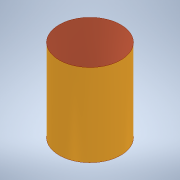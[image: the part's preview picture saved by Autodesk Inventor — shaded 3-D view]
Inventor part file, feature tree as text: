
AUTODESK INVENTOR PART (.ipt)
format: ipt  version: 2020.1 (Build 241239000, 239)  size: 92,672 bytes
history: native  units: mm
features: extrude x1, sketch x1
ambient origin geometry x8: Origin, YZ Plane, XZ Plane, XY Plane, X Axis, Y Axis, Z Axis, Center Point
bodies: Solid1 (feature_tree)
feature tree (2):
  extrude  "Extrusion1"  Depth=50.8mm TaperAngle=0.0deg
  sketch  "Sketch1"  dims[d0=37.846mm d1=50.8mm d2=0.0mm]
